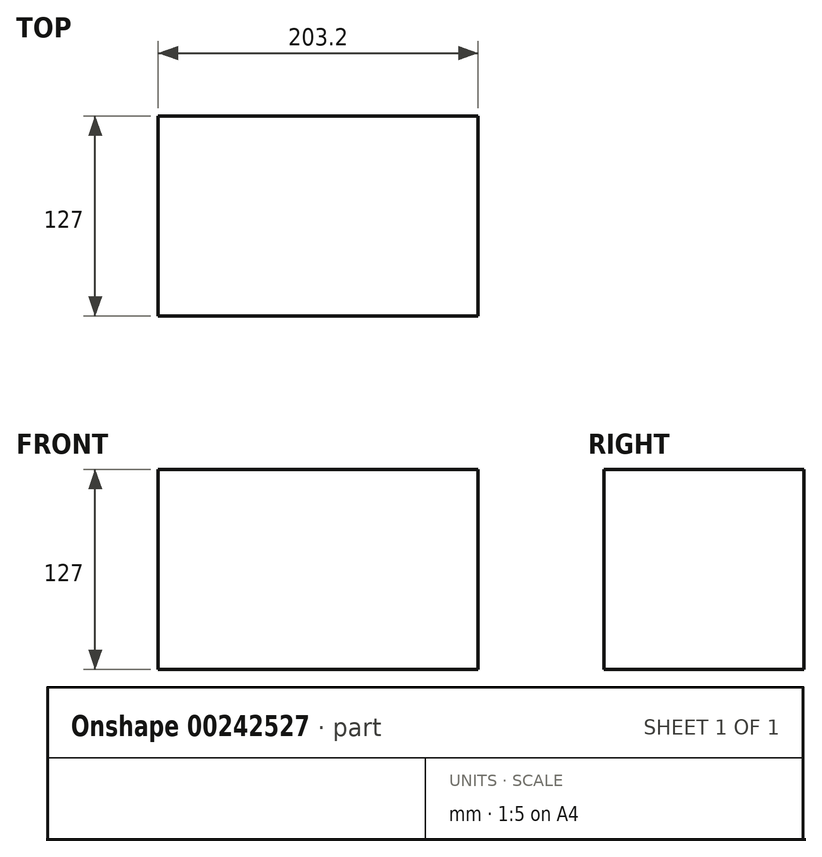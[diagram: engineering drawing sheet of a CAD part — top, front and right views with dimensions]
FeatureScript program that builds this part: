
annotation { "Feature Type Name" : "Feature", "Feature Type Description" : "" }
export const myFeature = defineFeature(function(context is Context, id is Id, definition is map)
    precondition{}
    {
        {
            var Q0;
            Q0=qCreatedBy(makeId("Front.planeOp"),FACE);
            var sketch = newSketch(context, id + "F0", { "sketchPlane" : qUnion([Q0])});
            skLineSegment(sketch, "E0.bottom", {"start": v(-74.82, 85.25) * mm, "end": v(128.38, 85.25) * mm});
            skLineSegment(sketch, "E0.top", {"start": v(-74.82, -41.75) * mm, "end": v(128.38, -41.75) * mm});
            skLineSegment(sketch, "E0.left", {"start": v(-74.82, 85.25) * mm, "end": v(-74.82, -41.75) * mm});
            skLineSegment(sketch, "E0.right", {"start": v(128.38, 85.25) * mm, "end": v(128.38, -41.75) * mm});
            skSolve(sketch);
        }
        {
            var Q0;
            Q0 = qSketchRegion(id + "F0", true);
            extrude(context, id + "F1", {"entities" : qUnion([Q0]), "depth" : 127 * mm});
        }
    });
